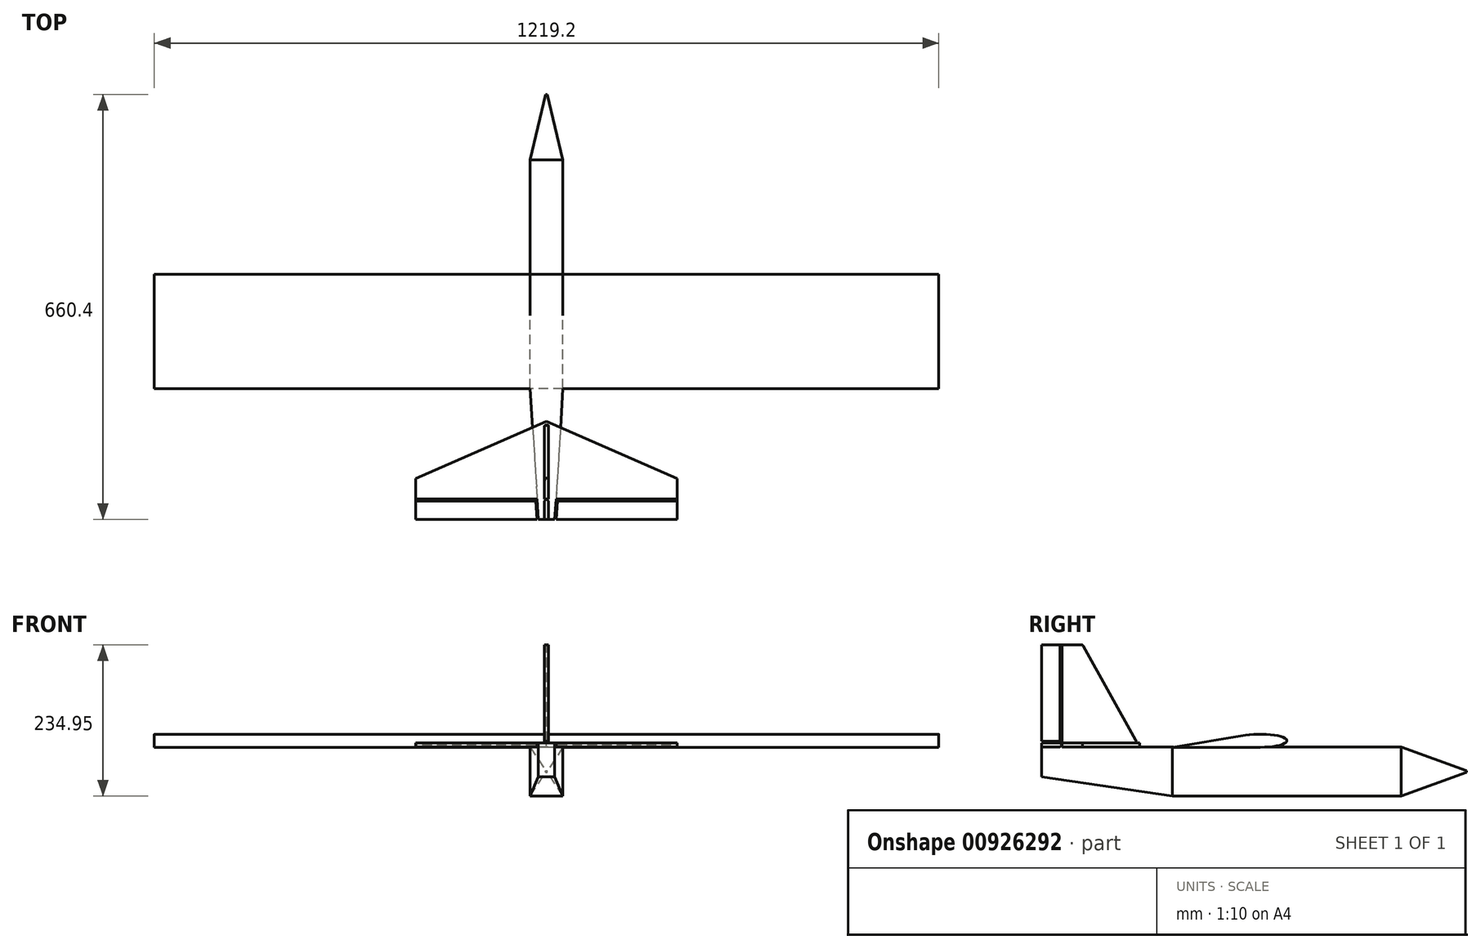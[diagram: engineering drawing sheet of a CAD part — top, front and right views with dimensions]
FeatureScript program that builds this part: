
annotation { "Feature Type Name" : "Feature", "Feature Type Description" : "" }
export const myFeature = defineFeature(function(context is Context, id is Id, definition is map)
    precondition{}
    {
        {
            var Q0;
            Q0=qCreatedBy(makeId("Front.planeOp"),FACE);
            var sketch = newSketch(context, id + "F0", { "sketchPlane" : qUnion([Q0])});
            skLineSegment(sketch, "E0.bottom", {"start": v(25.4, -38.1) * mm, "end": v(-25.4, -38.1) * mm});
            skLineSegment(sketch, "E0.top", {"start": v(25.4, 38.1) * mm, "end": v(-25.4, 38.1) * mm});
            skLineSegment(sketch, "E0.left", {"start": v(25.4, -38.1) * mm, "end": v(25.4, 38.1) * mm});
            skLineSegment(sketch, "E0.right", {"start": v(-25.4, -38.1) * mm, "end": v(-25.4, 38.1) * mm});
            skPoint(sketch, "E0.middle", {"position": v(0, 0) * mm});
            skSolve(sketch);
        }
        {
            var Q0;
            Q0 = qSketchRegion(id + "F0", true);
            extrude(context, id + "F1", {"entities" : qUnion([Q0]), "depth" : 355.6 * mm, "offsetDistance" : 25.4 * mm});
        }
        {
            var Q0;
            Q0=makeQuery(id+"F1.opExtrude","CAP_FACE",FACE,{"disambiguationData":[OSD([sQuery(id+"F0.wireOp",EDGE,"E0.bottom"),sQuery(id+"F0.wireOp",EDGE,"E0.top"),sQuery(id+"F0.wireOp",EDGE,"E0.left"),sQuery(id+"F0.wireOp",EDGE,"E0.right")])],"isStart":false});
            cPlane(context, id + "F2", {"entities" : qUnion([Q0]), "cplaneType" : CPlaneType.OFFSET, "offset" : 203.2 * mm, "width" : 152.4 * mm, "height" : 152.4 * mm});
        }
        {
            var Q0;
            Q0=qCreatedBy(id+"F2.planeOp",FACE);
            var sketch = newSketch(context, id + "F3", { "sketchPlane" : qUnion([Q0])});
            skLineSegment(sketch, "E1.bottom", {"start": v(12.69, -8.14) * mm, "end": v(-12.69, -8.14) * mm});
            skLineSegment(sketch, "E1.top", {"start": v(12.69, 38.1) * mm, "end": v(-12.69, 38.1) * mm});
            skLineSegment(sketch, "E1.left", {"start": v(12.69, -8.14) * mm, "end": v(12.69, 38.1) * mm});
            skLineSegment(sketch, "E1.right", {"start": v(-12.69, -8.14) * mm, "end": v(-12.69, 38.1) * mm});
            skPoint(sketch, "E1.middle", {"position": v(0, 14.98) * mm});
            skSolve(sketch);
        }
        {
            var Q1;
            Q1=makeQuery(id+"F1.opExtrude","CAP_FACE",FACE,{"disambiguationData":[OSD([sQuery(id+"F0.wireOp",EDGE,"E0.bottom"),sQuery(id+"F0.wireOp",EDGE,"E0.top"),sQuery(id+"F0.wireOp",EDGE,"E0.left"),sQuery(id+"F0.wireOp",EDGE,"E0.right")])],"isStart":false});
            var Q2;
            Q2=makeQuery(id+"F3.imprint","IMPRINT",FACE,{"disambiguationData":[TD([[makeQuery(id+"F3.imprint","IMPRINT",EDGE,{"derivedFrom":sQuery(id+"F3.wireOp",EDGE,"E1.bottom")}),-1.0]])]});
            loft(context, id + "F4", {"operationType" : NewBodyOperationType.ADD, "sheetProfilesArray" : [{ "sheetProfileEntities" : qUnion([Q1]) }, { "sheetProfileEntities" : qUnion([Q2]) }]});
        }
        {
            var Q0;
            Q0=qCreatedBy(makeId("Right.planeOp"),FACE);
            var sketch = newSketch(context, id + "F5", { "sketchPlane" : qUnion([Q0])});
            skEllipse(sketch, "E2", {"center": v(-219.08, 47.95) * mm, "majorRadius": 41.28 * mm, "minorRadius": 10.16 * mm, "majorAxis": v(-1, 0)});
            skLineSegment(sketch, "E3", {"start": v(-219.08, 37.8) * mm, "end": v(-355.6, 37.8) * mm});
            skLineSegment(sketch, "E4", {"start": v(-355.6, 37.8) * mm, "end": v(-241.94, 56.41) * mm});
            skLineSegment(sketch, "E5", {"start": v(-177.8, 47.95) * mm, "end": v(-260.35, 47.95) * mm, "construction": true});
            skLineSegment(sketch, "E6", {"start": v(-177.8, 47.95) * mm, "end": v(-355.6, 37.8) * mm, "construction": true});
            skSolve(sketch);
        }
        {
            var Q0;
            Q0 = qSketchRegion(id + "F5", true);
            extrude(context, id + "F6", {"entities" : qUnion([Q0]), "depth" : 1219.2 * mm, "offsetDistance" : 25.4 * mm, "symmetric" : true});
        }
        {
            var Q0;
            Q0=qCreatedBy(makeId("Right.planeOp"),FACE);
            var sketch = newSketch(context, id + "F7", { "sketchPlane" : qUnion([Q0])});
            skLineSegment(sketch, "E7.bottom", {"start": v(-558.8, 38.1) * mm, "end": v(-406.4, 38.1) * mm});
            skLineSegment(sketch, "E7.top", {"start": v(-558.8, 44.45) * mm, "end": v(-406.4, 44.45) * mm});
            skLineSegment(sketch, "E7.left", {"start": v(-558.8, 38.1) * mm, "end": v(-558.8, 44.45) * mm});
            skLineSegment(sketch, "E7.right", {"start": v(-406.4, 38.1) * mm, "end": v(-406.4, 44.45) * mm});
            skSolve(sketch);
        }
        {
            var Q0;
            Q0=makeQuery(id+"F7.imprint","IMPRINT",FACE,{"disambiguationData":[TD([[makeQuery(id+"F7.imprint","IMPRINT",EDGE,{"derivedFrom":sQuery(id+"F7.wireOp",EDGE,"E7.bottom")}),1.0]])]});
            cPlane(context, id + "F8", {"entities" : qUnion([Q0]), "cplaneType" : CPlaneType.OFFSET, "offset" : 203.2 * mm, "width" : 152.4 * mm, "height" : 152.4 * mm});
        }
        {
            var Q0;
            Q0=qCreatedBy(id+"F8.planeOp",FACE);
            var sketch = newSketch(context, id + "F9", { "sketchPlane" : qUnion([Q0])});
            skLineSegment(sketch, "E8.bottom", {"start": v(-558.8, 44.45) * mm, "end": v(-495.3, 44.45) * mm});
            skLineSegment(sketch, "E8.top", {"start": v(-558.8, 38.1) * mm, "end": v(-495.3, 38.1) * mm});
            skLineSegment(sketch, "E8.left", {"start": v(-558.8, 44.45) * mm, "end": v(-558.8, 38.1) * mm});
            skLineSegment(sketch, "E8.right", {"start": v(-495.3, 44.45) * mm, "end": v(-495.3, 38.1) * mm});
            skSolve(sketch);
        }
        {
            var Q1;
            Q1=makeQuery(id+"F7.imprint","IMPRINT",FACE,{"disambiguationData":[TD([[makeQuery(id+"F7.imprint","IMPRINT",EDGE,{"derivedFrom":sQuery(id+"F7.wireOp",EDGE,"E7.bottom")}),1.0]])]});
            var Q2;
            Q2=makeQuery(id+"F9.imprint","IMPRINT",FACE,{"disambiguationData":[TD([[makeQuery(id+"F9.imprint","IMPRINT",EDGE,{"derivedFrom":sQuery(id+"F9.wireOp",EDGE,"E8.bottom")}),-1.0]])]});
            loft(context, id + "F10", {"sheetProfilesArray" : [{ "sheetProfileEntities" : qUnion([Q1]) }, { "sheetProfileEntities" : qUnion([Q2]) }]});
        }
        {
            var Q0;
            Q0=makeQuery(id+"F10.opLoft","SWEPT_BODY",BODY,{"disambiguationData":[OSD([makeQuery(id+"F7.imprint","IMPRINT",FACE,{"disambiguationData":[TD([[makeQuery(id+"F7.imprint","IMPRINT",EDGE,{"derivedFrom":sQuery(id+"F7.wireOp",EDGE,"E7.bottom")}),1.0]])]}),makeQuery(id+"F9.imprint","IMPRINT",FACE,{"disambiguationData":[TD([[makeQuery(id+"F9.imprint","IMPRINT",EDGE,{"derivedFrom":sQuery(id+"F9.wireOp",EDGE,"E8.bottom")}),-1.0]])]})])]});
            var Q1;
            Q1=makeQuery(id+"F10.opLoft","CAP_FACE",FACE,{"disambiguationData":[OSD([makeQuery(id+"F7.imprint","IMPRINT",FACE,{"disambiguationData":[TD([[makeQuery(id+"F7.imprint","IMPRINT",EDGE,{"derivedFrom":sQuery(id+"F7.wireOp",EDGE,"E7.bottom")}),1.0]])]})])],"isStart":true});
            mirror(context, id + "F11", {"operationType" : NewBodyOperationType.ADD, "entities" : qUnion([Q0]), "mirrorPlane" : qUnion([Q1])});
        }
        {
            var Q0;
            {var subQ0=makeQuery(id+"F10.opLoft","SWEPT_FACE",FACE,{"disambiguationData":[OSD([sQuery(id+"F7.wireOp",EDGE,"E7.top"),sQuery(id+"F7.wireOp",EDGE,"E7.left"),sQuery(id+"F7.wireOp",EDGE,"E7.right"),sQuery(id+"F9.wireOp",EDGE,"E8.bottom"),sQuery(id+"F9.wireOp",EDGE,"E8.left"),sQuery(id+"F9.wireOp",EDGE,"E8.right")])]});Q0=makeQuery(id+"F11.boolean.opBoolean","MERGE",FACE,{"derivedFrom":[subQ0,makeQuery(id+"F11.opPattern","COPY",FACE,{"derivedFrom":subQ0,"instanceName":"1"})]});}
            var sketch = newSketch(context, id + "F12", { "sketchPlane" : qUnion([Q0])});
            skLineSegment(sketch, "E9.bottom", {"start": v(3.18, -558.8) * mm, "end": v(-3.17, -558.8) * mm});
            skLineSegment(sketch, "E9.top", {"start": v(3.18, -410.21) * mm, "end": v(-3.17, -410.21) * mm});
            skLineSegment(sketch, "E9.left", {"start": v(3.18, -558.8) * mm, "end": v(3.18, -410.21) * mm});
            skLineSegment(sketch, "E9.right", {"start": v(-3.17, -558.8) * mm, "end": v(-3.17, -410.21) * mm});
            skPoint(sketch, "E9.middle", {"position": v(0, -484.5) * mm});
            skSolve(sketch);
        }
        {
            var Q0;
            Q0=makeQuery(id+"F12.imprint","IMPRINT",FACE,{"disambiguationData":[TD([[makeQuery(id+"F12.imprint","IMPRINT",EDGE,{"derivedFrom":sQuery(id+"F12.wireOp",EDGE,"E9.top")}),-1.0]])]});
            cPlane(context, id + "F13", {"entities" : qUnion([Q0]), "cplaneType" : CPlaneType.OFFSET, "offset" : 152.4 * mm, "width" : 152.4 * mm, "height" : 152.4 * mm});
        }
        {
            var Q0;
            Q0=qCreatedBy(id+"F13.planeOp",FACE);
            var sketch = newSketch(context, id + "F14", { "sketchPlane" : qUnion([Q0])});
            skLineSegment(sketch, "E10.bottom", {"start": v(-3.17, -558.8) * mm, "end": v(3.18, -558.8) * mm});
            skLineSegment(sketch, "E10.top", {"start": v(-3.17, -495.3) * mm, "end": v(3.18, -495.3) * mm});
            skLineSegment(sketch, "E10.left", {"start": v(-3.17, -558.8) * mm, "end": v(-3.17, -495.3) * mm});
            skLineSegment(sketch, "E10.right", {"start": v(3.18, -558.8) * mm, "end": v(3.18, -495.3) * mm});
            skPoint(sketch, "E10.middle", {"position": v(0, -527.05) * mm});
            skSolve(sketch);
        }
        {
            var Q1;
            Q1=makeQuery(id+"F12.imprint","IMPRINT",FACE,{"disambiguationData":[TD([[makeQuery(id+"F12.imprint","IMPRINT",EDGE,{"derivedFrom":sQuery(id+"F12.wireOp",EDGE,"E9.bottom")}),1.0]])]});
            var Q2;
            Q2=makeQuery(id+"F14.imprint","IMPRINT",FACE,{"disambiguationData":[TD([[makeQuery(id+"F14.imprint","IMPRINT",EDGE,{"derivedFrom":sQuery(id+"F14.wireOp",EDGE,"E10.bottom")}),1.0]])]});
            loft(context, id + "F15", {"sheetProfilesArray" : [{ "sheetProfileEntities" : qUnion([Q1]) }, { "sheetProfileEntities" : qUnion([Q2]) }]});
        }
        {
            var Q0;
            Q0=makeQuery(id+"F1.opExtrude","CAP_FACE",FACE,{"disambiguationData":[OSD([sQuery(id+"F0.wireOp",EDGE,"E0.bottom"),sQuery(id+"F0.wireOp",EDGE,"E0.top"),sQuery(id+"F0.wireOp",EDGE,"E0.left"),sQuery(id+"F0.wireOp",EDGE,"E0.right")])],"isStart":true});
            cPlane(context, id + "F16", {"entities" : qUnion([Q0]), "cplaneType" : CPlaneType.OFFSET, "offset" : 101.6 * mm, "width" : 152.4 * mm, "height" : 152.4 * mm});
        }
        {
            var Q0;
            Q0=qCreatedBy(id+"F16.planeOp",FACE);
            var sketch = newSketch(context, id + "F17", { "sketchPlane" : qUnion([Q0])});
            skLineSegment(sketch, "E11.bottom", {"start": v(1.27, -1.27) * mm, "end": v(-1.27, -1.27) * mm});
            skLineSegment(sketch, "E11.top", {"start": v(1.27, 1.27) * mm, "end": v(-1.27, 1.27) * mm});
            skLineSegment(sketch, "E11.left", {"start": v(1.27, -1.27) * mm, "end": v(1.27, 1.27) * mm});
            skLineSegment(sketch, "E11.right", {"start": v(-1.27, -1.27) * mm, "end": v(-1.27, 1.27) * mm});
            skPoint(sketch, "E11.middle", {"position": v(0, 0) * mm});
            skSolve(sketch);
        }
        {
            var Q1;
            Q1=makeQuery(id+"F1.opExtrude","CAP_FACE",FACE,{"disambiguationData":[OSD([sQuery(id+"F0.wireOp",EDGE,"E0.bottom"),sQuery(id+"F0.wireOp",EDGE,"E0.top"),sQuery(id+"F0.wireOp",EDGE,"E0.left"),sQuery(id+"F0.wireOp",EDGE,"E0.right")])],"isStart":true});
            var Q2;
            Q2=makeQuery(id+"F17.imprint","IMPRINT",FACE,{"disambiguationData":[TD([[makeQuery(id+"F17.imprint","IMPRINT",EDGE,{"derivedFrom":sQuery(id+"F17.wireOp",EDGE,"E11.bottom")}),-1.0]])]});
            loft(context, id + "F18", {"operationType" : NewBodyOperationType.ADD, "sheetProfilesArray" : [{ "sheetProfileEntities" : qUnion([Q1]) }, { "sheetProfileEntities" : qUnion([Q2]) }]});
        }
        {
            var Q0;
            Q0=makeQuery(id+"F15.opLoft","SWEPT_FACE",FACE,{"disambiguationData":[OSD([sQuery(id+"F12.wireOp",EDGE,"E9.top"),sQuery(id+"F12.wireOp",EDGE,"E9.left"),sQuery(id+"F12.wireOp",EDGE,"E9.right"),sQuery(id+"F14.wireOp",EDGE,"E10.top"),sQuery(id+"F14.wireOp",EDGE,"E10.left"),sQuery(id+"F14.wireOp",EDGE,"E10.right")])]});
            var Q1;
            Q1=makeQuery(id+"F10.opLoft","SWEPT_FACE",FACE,{"disambiguationData":[OSD([sQuery(id+"F7.wireOp",EDGE,"E7.bottom"),sQuery(id+"F7.wireOp",EDGE,"E7.top"),sQuery(id+"F7.wireOp",EDGE,"E7.right"),sQuery(id+"F9.wireOp",EDGE,"E8.bottom"),sQuery(id+"F9.wireOp",EDGE,"E8.top"),sQuery(id+"F9.wireOp",EDGE,"E8.right")])]});
            var Q2;
            Q2=makeQuery(id+"F11.opPattern","COPY",FACE,{"derivedFrom":makeQuery(id+"F10.opLoft","SWEPT_FACE",FACE,{"disambiguationData":[OSD([sQuery(id+"F7.wireOp",EDGE,"E7.bottom"),sQuery(id+"F7.wireOp",EDGE,"E7.top"),sQuery(id+"F7.wireOp",EDGE,"E7.right"),sQuery(id+"F9.wireOp",EDGE,"E8.bottom"),sQuery(id+"F9.wireOp",EDGE,"E8.top"),sQuery(id+"F9.wireOp",EDGE,"E8.right")])]}),"instanceName":"1"});
            fillet(context, id + "F19", {"entities" : qUnion([Q0, Q1, Q2]), "radius" : 3.05 * mm, "tangentPropagation" : true, "allowEdgeOverflow" : false});
        }
        {
            var Q0;
            Q0=makeQuery(id+"F15.opLoft","CAP_FACE",FACE,{"disambiguationData":[OSD([makeQuery(id+"F14.imprint","IMPRINT",FACE,{"disambiguationData":[TD([[makeQuery(id+"F14.imprint","IMPRINT",EDGE,{"derivedFrom":sQuery(id+"F14.wireOp",EDGE,"E10.bottom")}),1.0]])]})])],"isStart":true});
            var sketch = newSketch(context, id + "F20", { "sketchPlane" : qUnion([Q0])});
            skLineSegment(sketch, "E12", {"start": v(0, -527.05) * mm, "end": v(0, -558.8) * mm, "construction": true});
            skLineSegment(sketch, "E13", {"start": v(0, -527.05) * mm, "end": v(3.18, -527.05) * mm});
            skLineSegment(sketch, "E14", {"start": v(3.18, -527.05) * mm, "end": v(3.18, -530.22) * mm});
            skLineSegment(sketch, "E15", {"start": v(3.18, -530.22) * mm, "end": v(0, -527.05) * mm});
            skLineSegment(sketch, "E16.MirrorCS", {"start": v(-3.18, -527.05) * mm, "end": v(-3.18, -530.22) * mm});
            skLineSegment(sketch, "E17.MirrorCS", {"start": v(-3.17, -530.22) * mm, "end": v(0, -527.05) * mm});
            skLineSegment(sketch, "E18.MirrorCS", {"start": v(0, -527.05) * mm, "end": v(-3.17, -527.05) * mm});
            skSolve(sketch);
        }
        {
            var Q0;
            Q0=makeQuery(id+"F20.imprint","IMPRINT",FACE,{"disambiguationData":[TD([[makeQuery(id+"F20.imprint","IMPRINT",EDGE,{"derivedFrom":sQuery(id+"F20.wireOp",EDGE,"E16.MirrorCS")}),1.0]])]});
            var Q1;
            {var subQ0=makeQuery(id+"F10.opLoft","SWEPT_FACE",FACE,{"disambiguationData":[OSD([sQuery(id+"F7.wireOp",EDGE,"E7.top"),sQuery(id+"F7.wireOp",EDGE,"E7.left"),sQuery(id+"F7.wireOp",EDGE,"E7.right"),sQuery(id+"F9.wireOp",EDGE,"E8.bottom"),sQuery(id+"F9.wireOp",EDGE,"E8.left"),sQuery(id+"F9.wireOp",EDGE,"E8.right")])]});Q1=makeQuery(id+"F11.boolean.opBoolean","MERGE",FACE,{"derivedFrom":[subQ0,makeQuery(id+"F11.opPattern","COPY",FACE,{"derivedFrom":subQ0,"instanceName":"1"})]});}
            extrude(context, id + "F21", {"entities" : qUnion([Q0]), "operationType" : NewBodyOperationType.REMOVE, "endBound" : BoundingType.UP_TO_SURFACE, "oppositeDirection" : true, "depth" : 25.4 * mm, "endBoundEntityFace" : qUnion([Q1]), "offsetDistance" : 25.4 * mm});
        }
        {
            var Q0;
            Q0=makeQuery(id+"F20.imprint","IMPRINT",FACE,{"disambiguationData":[TD([[makeQuery(id+"F20.imprint","IMPRINT",EDGE,{"derivedFrom":sQuery(id+"F20.wireOp",EDGE,"E13")}),-1.0]])]});
            var Q1;
            {var subQ0=makeQuery(id+"F10.opLoft","SWEPT_FACE",FACE,{"disambiguationData":[OSD([sQuery(id+"F7.wireOp",EDGE,"E7.top"),sQuery(id+"F7.wireOp",EDGE,"E7.left"),sQuery(id+"F7.wireOp",EDGE,"E7.right"),sQuery(id+"F9.wireOp",EDGE,"E8.bottom"),sQuery(id+"F9.wireOp",EDGE,"E8.left"),sQuery(id+"F9.wireOp",EDGE,"E8.right")])]});Q1=makeQuery(id+"F11.boolean.opBoolean","MERGE",FACE,{"derivedFrom":[subQ0,makeQuery(id+"F11.opPattern","COPY",FACE,{"derivedFrom":subQ0,"instanceName":"1"})]});}
            extrude(context, id + "F22", {"entities" : qUnion([Q0]), "operationType" : NewBodyOperationType.REMOVE, "endBound" : BoundingType.UP_TO_SURFACE, "oppositeDirection" : true, "depth" : 25.4 * mm, "endBoundEntityFace" : qUnion([Q1]), "offsetDistance" : 25.4 * mm});
        }
        {
            var Q0;
            Q0=makeQuery(id+"F15.opLoft","SWEPT_FACE",FACE,{"disambiguationData":[OSD([sQuery(id+"F7.wireOp",EDGE,"E7.top"),sQuery(id+"F7.wireOp",EDGE,"E7.left"),sQuery(id+"F9.wireOp",EDGE,"E8.bottom"),sQuery(id+"F9.wireOp",EDGE,"E8.left"),sQuery(id+"F12.wireOp",EDGE,"E9.bottom"),sQuery(id+"F12.wireOp",EDGE,"E9.left"),sQuery(id+"F12.wireOp",EDGE,"E9.right"),sQuery(id+"F14.wireOp",EDGE,"E10.bottom"),sQuery(id+"F14.wireOp",EDGE,"E10.left"),sQuery(id+"F14.wireOp",EDGE,"E10.right")])]});
            var sketch = newSketch(context, id + "F23", { "sketchPlane" : qUnion([Q0])});
            skLineSegment(sketch, "E19.bottom", {"start": v(-3.17, 44.45) * mm, "end": v(3.18, 44.45) * mm});
            skLineSegment(sketch, "E19.top", {"start": v(-3.17, 46.99) * mm, "end": v(3.18, 46.99) * mm});
            skLineSegment(sketch, "E19.left", {"start": v(-3.17, 44.45) * mm, "end": v(-3.17, 46.99) * mm});
            skLineSegment(sketch, "E19.right", {"start": v(3.18, 44.45) * mm, "end": v(3.18, 46.99) * mm});
            skSolve(sketch);
        }
        {
            var Q0;
            Q0 = qSketchRegion(id + "F23", true);
            var Q1;
            Q1=makeQuery(id+"F22.boolean.opBoolean","MERGE",FACE,{"derivedFrom":[makeQuery(id+"F21.boolean.opBoolean","COPY",FACE,{"derivedFrom":makeQuery(id+"F21.opExtrude","SWEPT_FACE",FACE,{"disambiguationData":[OSD([sQuery(id+"F20.wireOp",EDGE,"E18.MirrorCS")])]})})],"fromTools":[makeQuery(id+"F22.opExtrude","SWEPT_FACE",FACE,{"disambiguationData":[OSD([sQuery(id+"F20.wireOp",EDGE,"E13")])]})]});
            extrude(context, id + "F24", {"entities" : qUnion([Q0]), "operationType" : NewBodyOperationType.REMOVE, "endBound" : BoundingType.UP_TO_SURFACE, "oppositeDirection" : true, "depth" : 25.4 * mm, "endBoundEntityFace" : qUnion([Q1]), "offsetDistance" : 25.4 * mm});
        }
        {
            var Q0;
            Q0=makeQuery(id+"F10.opLoft","CAP_FACE",FACE,{"disambiguationData":[OSD([makeQuery(id+"F9.imprint","IMPRINT",FACE,{"disambiguationData":[TD([[makeQuery(id+"F9.imprint","IMPRINT",EDGE,{"derivedFrom":sQuery(id+"F9.wireOp",EDGE,"E8.bottom")}),-1.0]])]})])],"isStart":true});
            var sketch = newSketch(context, id + "F25", { "sketchPlane" : qUnion([Q0])});
            skLineSegment(sketch, "E20", {"start": v(-558.8, 41.27) * mm, "end": v(-527.05, 41.27) * mm, "construction": true});
            skLineSegment(sketch, "E21", {"start": v(-527.05, 44.45) * mm, "end": v(-527.05, 41.34) * mm});
            skLineSegment(sketch, "E22", {"start": v(-527.11, 41.34) * mm, "end": v(-530.23, 44.45) * mm});
            skLineSegment(sketch, "E23", {"start": v(-530.23, 44.45) * mm, "end": v(-527.05, 44.45) * mm});
            skLineSegment(sketch, "E24.MirrorCS", {"start": v(-527.11, 41.21) * mm, "end": v(-530.23, 38.1) * mm});
            skLineSegment(sketch, "E25.MirrorCS", {"start": v(-527.05, 38.1) * mm, "end": v(-527.05, 41.21) * mm});
            skLineSegment(sketch, "E26.MirrorCS", {"start": v(-530.23, 38.1) * mm, "end": v(-527.05, 38.1) * mm});
            skLineSegment(sketch, "E27.bottom", {"start": v(-527.05, 41.34) * mm, "end": v(-527.11, 41.34) * mm});
            skLineSegment(sketch, "E27.top", {"start": v(-527.05, 41.21) * mm, "end": v(-527.11, 41.21) * mm});
            skPoint(sketch, "E28.orphan", {"position": v(-527.05, 41.27) * mm});
            skSolve(sketch);
        }
        {
            var Q0;
            Q0=makeQuery(id+"F25.imprint","IMPRINT",FACE,{"disambiguationData":[TD([[makeQuery(id+"F25.imprint","IMPRINT",EDGE,{"derivedFrom":sQuery(id+"F25.wireOp",EDGE,"E21")}),-1.0]])]});
            var Q1;
            Q1=makeQuery(id+"F25.imprint","IMPRINT",FACE,{"disambiguationData":[TD([[makeQuery(id+"F25.imprint","IMPRINT",EDGE,{"derivedFrom":sQuery(id+"F25.wireOp",EDGE,"E24.MirrorCS")}),1.0]])]});
            var Q2;
            Q2=makeQuery(id+"F4.opLoft","SWEPT_FACE",FACE,{"disambiguationData":[OSD([sQuery(id+"F0.wireOp",EDGE,"E0.bottom"),sQuery(id+"F0.wireOp",EDGE,"E0.top"),sQuery(id+"F0.wireOp",EDGE,"E0.left"),sQuery(id+"F3.wireOp",EDGE,"E1.bottom"),sQuery(id+"F3.wireOp",EDGE,"E1.top"),sQuery(id+"F3.wireOp",EDGE,"E1.left")])]});
            extrude(context, id + "F26", {"entities" : qUnion([Q0, Q1]), "operationType" : NewBodyOperationType.REMOVE, "endBound" : BoundingType.UP_TO_SURFACE, "oppositeDirection" : true, "depth" : 25.4 * mm, "endBoundEntityFace" : qUnion([Q2]), "offsetDistance" : 25.4 * mm});
        }
        {
            var Q0;
            Q0=makeQuery(id+"F11.opPattern","COPY",FACE,{"derivedFrom":makeQuery(id+"F10.opLoft","CAP_FACE",FACE,{"disambiguationData":[OSD([makeQuery(id+"F9.imprint","IMPRINT",FACE,{"disambiguationData":[TD([[makeQuery(id+"F9.imprint","IMPRINT",EDGE,{"derivedFrom":sQuery(id+"F9.wireOp",EDGE,"E8.bottom")}),-1.0]])]})])],"isStart":true}),"instanceName":"1"});
            var sketch = newSketch(context, id + "F27", { "sketchPlane" : qUnion([Q0])});
            skLineSegment(sketch, "E29.0", {"start": v(527.05, 44.45) * mm, "end": v(527.05, 41.34) * mm});
            skLineSegment(sketch, "E30.0", {"start": v(527.11, 41.34) * mm, "end": v(530.23, 44.45) * mm});
            skLineSegment(sketch, "E31.0", {"start": v(527.11, 41.21) * mm, "end": v(530.23, 38.1) * mm});
            skLineSegment(sketch, "E32.0", {"start": v(527.05, 38.1) * mm, "end": v(527.05, 41.21) * mm});
            skLineSegment(sketch, "E33.0", {"start": v(530.23, 38.1) * mm, "end": v(527.05, 38.1) * mm});
            skLineSegment(sketch, "E34.0", {"start": v(530.23, 44.45) * mm, "end": v(527.05, 44.45) * mm});
            skPoint(sketch, "E35.0", {"position": v(527.08, 41.34) * mm});
            skLineSegment(sketch, "E36.0", {"start": v(527.05, 41.34) * mm, "end": v(527.11, 41.34) * mm});
            skLineSegment(sketch, "E37.0", {"start": v(527.05, 41.21) * mm, "end": v(527.11, 41.21) * mm});
            skSolve(sketch);
        }
        {
            var Q0;
            Q0 = qSketchRegion(id + "F27", true);
            var Q1;
            Q1=makeQuery(id+"F4.opLoft","SWEPT_FACE",FACE,{"disambiguationData":[OSD([sQuery(id+"F0.wireOp",EDGE,"E0.bottom"),sQuery(id+"F0.wireOp",EDGE,"E0.top"),sQuery(id+"F0.wireOp",EDGE,"E0.right"),sQuery(id+"F3.wireOp",EDGE,"E1.bottom"),sQuery(id+"F3.wireOp",EDGE,"E1.top"),sQuery(id+"F3.wireOp",EDGE,"E1.right")])]});
            extrude(context, id + "F28", {"entities" : qUnion([Q0]), "operationType" : NewBodyOperationType.REMOVE, "endBound" : BoundingType.UP_TO_SURFACE, "oppositeDirection" : true, "depth" : 25.4 * mm, "endBoundEntityFace" : qUnion([Q1]), "offsetDistance" : 25.4 * mm});
        }
        {
            var Q0;
            {var subQ0=makeQuery(id+"F10.opLoft","SWEPT_FACE",FACE,{"disambiguationData":[OSD([sQuery(id+"F7.wireOp",EDGE,"E7.bottom"),sQuery(id+"F7.wireOp",EDGE,"E7.left"),sQuery(id+"F7.wireOp",EDGE,"E7.right"),sQuery(id+"F9.wireOp",EDGE,"E8.top"),sQuery(id+"F9.wireOp",EDGE,"E8.left"),sQuery(id+"F9.wireOp",EDGE,"E8.right")])]});Q0=makeQuery(id+"F11.boolean.opBoolean","MERGE",FACE,{"derivedFrom":[subQ0,makeQuery(id+"F11.opPattern","COPY",FACE,{"derivedFrom":subQ0,"instanceName":"1"})]});}
            var sketch = newSketch(context, id + "F29", { "sketchPlane" : qUnion([Q0])});
            skLineSegment(sketch, "E38", {"start": v(15.23, 558.8) * mm, "end": v(17.22, 527.05) * mm});
            skLineSegment(sketch, "E39", {"start": v(14.67, 527.05) * mm, "end": v(12.69, 558.8) * mm});
            skLineSegment(sketch, "E40", {"start": v(12.69, 558.8) * mm, "end": v(15.23, 558.8) * mm});
            skLineSegment(sketch, "E41.MirrorCS", {"start": v(-12.69, 558.8) * mm, "end": v(-15.23, 558.8) * mm});
            skLineSegment(sketch, "E42.MirrorCS", {"start": v(-15.23, 558.8) * mm, "end": v(-17.22, 527.05) * mm});
            skLineSegment(sketch, "E43.MirrorCS", {"start": v(-14.67, 527.05) * mm, "end": v(-12.69, 558.8) * mm});
            skLineSegment(sketch, "E44", {"start": v(14.67, 527.05) * mm, "end": v(17.22, 527.05) * mm});
            skLineSegment(sketch, "E45", {"start": v(-14.67, 527.05) * mm, "end": v(-17.22, 527.05) * mm});
            skSolve(sketch);
        }
        {
            var Q0;
            Q0 = qSketchRegion(id + "F29", true);
            var Q1;
            {var subQ0=makeQuery(id+"F10.opLoft","SWEPT_FACE",FACE,{"disambiguationData":[OSD([sQuery(id+"F7.wireOp",EDGE,"E7.top"),sQuery(id+"F7.wireOp",EDGE,"E7.left"),sQuery(id+"F7.wireOp",EDGE,"E7.right"),sQuery(id+"F9.wireOp",EDGE,"E8.bottom"),sQuery(id+"F9.wireOp",EDGE,"E8.left"),sQuery(id+"F9.wireOp",EDGE,"E8.right")])]});Q1=makeQuery(id+"F11.boolean.opBoolean","MERGE",FACE,{"derivedFrom":[subQ0,makeQuery(id+"F11.opPattern","COPY",FACE,{"derivedFrom":subQ0,"instanceName":"1"})]});}
            extrude(context, id + "F30", {"entities" : qUnion([Q0]), "operationType" : NewBodyOperationType.REMOVE, "endBound" : BoundingType.UP_TO_SURFACE, "oppositeDirection" : true, "depth" : 25.4 * mm, "endBoundEntityFace" : qUnion([Q1]), "offsetDistance" : 25.4 * mm});
        }
    });
